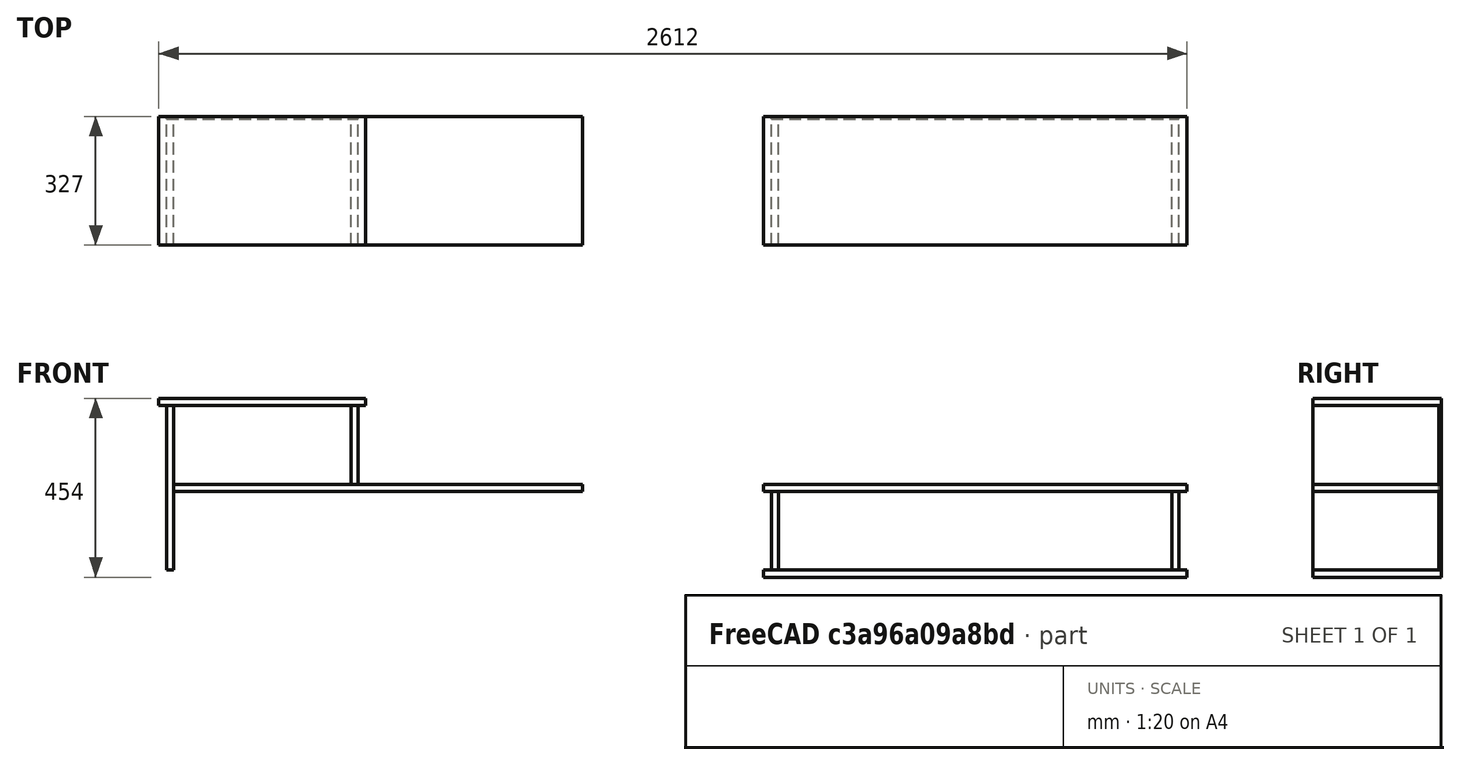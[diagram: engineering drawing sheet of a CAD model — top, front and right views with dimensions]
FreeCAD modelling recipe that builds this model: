
FCSTD DOCUMENT  (FreeCAD 0.20RUnknown)
Label: Brætspilsmøbel
License: All rights reserved
LicenseURL: http://en.wikipedia.org/wiki/All_rights_reserved
objects: Part::Box×7, Part::FeaturePython×6, Spreadsheet::Sheet×2, TechDraw::DrawSVGTemplate×1, TechDraw::DrawViewSpreadsheet×1, TechDraw::DrawPage×1
note: 13 computed .brp shape members not serialized (recipe doc carries the construction recipe); baked Part::Feature solids carry a one-line shape summary decoded from their .brp

FEATURE [Part::Box] panelYZ  label="Del1B2"
  AttacherType = Attacher::AttachEngine3D
  Height = 200
  Length = 486
  Placement = pos=(0,-7,236) rot=(0,0,1;0rad)
  Width = 7
  expr: .Placement.Base.y = -Spreadsheet.BagpladeT
  expr: .Placement.Base.z = <<maal>>.PladeT * 2 + <<maal>>.RumH
  expr: Height = <<maal>>.RumH
  expr: Length = <<maal>>.RumB + 2 * <<maal>>.PladeT
  expr: Width = Spreadsheet.BagpladeT
FEATURE [Spreadsheet::Sheet] Spreadsheet  label="maal"
  cells = A1=Rum b; B1=Rum h; C1=Rum d; D1=Plade tyk; E1=Bagplade tyk; F1=Underrum B; A2(RumB)==450mm; B2(RumH)==200mm; C2(RumD)==320mm; D2(PladeT)==18mm; E2(BagpladeT)==7mm; F2(UnderrumB)==1000mm; A5=Total bredde; B5=Total højde; C5=Total T; E5=OverUnderMarginB; A6(TotalB)==F2 + D2 * 2; B6(TotalH)==B2 * 2 + D2 * 3; C6(TotalT)==BagpladeT + RumD; E6(OverUnderMarginB)==20mm; A8=Del2X; A9(Del2X)==A6 + 500mm
FEATURE [Part::Box] panelZY  label="Del1L"
  AttacherType = Attacher::AttachEngine3D
  Height = 418
  Length = 18
  Placement = pos=(0,-327,18) rot=(0,0,1;0rad)
  Width = 320
  expr: .Placement.Base.y = -<<maal>>.TotalT
  expr: .Placement.Base.z = <<maal>>.PladeT
  expr: Height = <<maal>>.TotalH - <<maal>>.PladeT * 2
  expr: Length = <<maal>>.PladeT
  expr: Width = <<maal>>.RumD
FEATURE [Part::Box] panelXY  label="Del1U"
  AttacherType = Attacher::AttachEngine3D
  Height = 18
  Length = 1076
  Placement = pos=(-20,-327,0) rot=(0,0,1;0rad)
  Width = 327
  expr: .Placement.Base.x = -<<maal>>.OverUnderMarginB
  expr: .Placement.Base.y = -<<maal>>.TotalT
  expr: Height = <<maal>>.PladeT
  expr: Length = <<maal>>.TotalB + <<maal>>.OverUnderMarginB * 2
  expr: Width = <<maal>>.RumD + <<maal>>.BagpladeT
FEATURE [Part::Box] panelZY001  label="Del1R1"
  AttacherType = Attacher::AttachEngine3D
  Height = 200
  Length = 18
  Placement = pos=(1018,-327,18) rot=(0,0,1;0rad)
  Width = 320
  expr: .Placement.Base.x = <<maal>>.TotalB - <<maal>>.PladeT
  expr: .Placement.Base.y = -<<maal>>.TotalT
  expr: .Placement.Base.z = <<maal>>.PladeT
  expr: Height = <<maal>>.RumH
  expr: Length = <<maal>>.PladeT
  expr: Width = <<maal>>.RumD
FEATURE [Part::Box] panelXY001  label="Del1H"
  AttacherType = Attacher::AttachEngine3D
  Height = 18
  Length = 1038
  Placement = pos=(18,-327,218) rot=(0,0,1;0rad)
  Width = 327
  expr: .Placement.Base.x = <<maal>>.PladeT
  expr: .Placement.Base.y = -<<maal>>.TotalT
  expr: .Placement.Base.z = <<maal>>.RumH + <<maal>>.PladeT
  expr: Height = <<maal>>.PladeT
  expr: Length = <<maal>>.TotalB - <<maal>>.PladeT + <<maal>>.OverUnderMarginB
  expr: Width = <<maal>>.RumD + <<maal>>.BagpladeT
FEATURE [Part::FeaturePython] Clone  label="Del1R2"  # Draft clone (typed FeaturePython)
  AttacherType = Attacher::AttachEngine3D
  Fuse = false
  Objects = -> [panelZY001]
  Placement = pos=(468,-327,236) rot=(0,0,1;0rad)
  Scale = (1,1,1)
  expr: .Placement.Base.x = <<maal>>.RumB + <<maal>>.PladeT
  expr: .Placement.Base.y = -<<maal>>.BagpladeT - <<maal>>.RumD
  expr: .Placement.Base.z = <<maal>>.RumH + <<maal>>.PladeT * 2
FEATURE [Part::Box] panelXY002  label="Del1O"
  AttacherType = Attacher::AttachEngine3D
  Height = 18
  Length = 526
  Placement = pos=(-20,-327,436) rot=(0,0,1;0rad)
  Width = 327
  expr: .Placement.Base.x = -<<maal>>.OverUnderMarginB
  expr: .Placement.Base.y = -<<maal>>.TotalT
  expr: .Placement.Base.z = <<maal>>.TotalH - <<maal>>.PladeT
  expr: Height = <<maal>>.PladeT
  expr: Length = <<maal>>.RumB + <<maal>>.PladeT * 2 + <<maal>>.OverUnderMarginB * 2
  expr: Width = <<maal>>.RumD + <<maal>>.BagpladeT
FEATURE [Part::Box] panelYZ001  label="Del1B1"
  AttacherType = Attacher::AttachEngine3D
  Height = 200
  Length = 1036
  Placement = pos=(0,-7,18) rot=(0,0,1;0rad)
  Width = 7
  expr: .Placement.Base.y = -Spreadsheet.BagpladeT
  expr: .Placement.Base.z = <<maal>>.PladeT
  expr: Height = <<maal>>.RumH
  expr: Length = <<maal>>.TotalB
  expr: Width = Spreadsheet.BagpladeT
FEATURE [Part::FeaturePython] Clone001  label="Del2U"  # Draft clone (typed FeaturePython)
  AttacherType = Attacher::AttachEngine3D
  Fuse = false
  Objects = -> [panelXY]
  Placement = pos=(1516,-327,0) rot=(0,0,1;0rad)
  Scale = (1,1,1)
  expr: .Placement.Base.x = <<maal>>.Del2X - <<maal>>.OverUnderMarginB
  expr: .Placement.Base.y = -<<maal>>.BagpladeT - <<maal>>.RumD
FEATURE [Part::FeaturePython] Clone002  label="Del2O"  # Draft clone (typed FeaturePython)
  AttacherType = Attacher::AttachEngine3D
  Fuse = false
  Objects = -> [panelXY]
  Placement = pos=(1516,-327,218) rot=(0,0,1;0rad)
  Scale = (1,1,1)
  expr: .Placement.Base.x = <<maal>>.Del2X - <<maal>>.OverUnderMarginB
  expr: .Placement.Base.y = -<<maal>>.BagpladeT - <<maal>>.RumD
  expr: .Placement.Base.z = <<maal>>.RumH + <<maal>>.PladeT
FEATURE [Part::FeaturePython] Clone003  label="Del2L"  # Draft clone (typed FeaturePython)
  AttacherType = Attacher::AttachEngine3D
  Fuse = false
  Objects = -> [panelZY001]
  Placement = pos=(1536,-327,18) rot=(0,0,1;0rad)
  Scale = (1,1,1)
  expr: .Placement.Base.x = <<maal>>.Del2X
  expr: .Placement.Base.y = -<<maal>>.BagpladeT - <<maal>>.RumD
  expr: .Placement.Base.z = <<maal>>.PladeT
FEATURE [Part::FeaturePython] Clone004  label="Del2R"  # Draft clone (typed FeaturePython)
  AttacherType = Attacher::AttachEngine3D
  Fuse = false
  Objects = -> [panelZY001]
  Placement = pos=(2554,-327,18) rot=(0,0,1;0rad)
  Scale = (1,1,1)
  expr: .Placement.Base.x = <<maal>>.Del2X + <<maal>>.UnderrumB + <<maal>>.PladeT
  expr: .Placement.Base.y = -<<maal>>.BagpladeT - <<maal>>.RumD
  expr: .Placement.Base.z = <<maal>>.PladeT
FEATURE [Part::FeaturePython] Clone005  label="Del2B"  # Draft clone (typed FeaturePython)
  AttacherType = Attacher::AttachEngine3D
  Fuse = false
  Objects = -> [panelYZ001]
  Placement = pos=(1536,-7,18) rot=(0,0,1;0rad)
  Scale = (1,1,1)
  expr: .Placement.Base.x = <<maal>>.Del2X
  expr: .Placement.Base.y = -<<maal>>.BagpladeT
  expr: .Placement.Base.z = <<maal>>.PladeT
FEATURE [Spreadsheet::Sheet] toCut
  cells = A1=Quantity; C1=Dimensions; F1=Thickness; G1=m2; A2=1 x; C2=200 mm; D2=x; E2=486 mm; F2=7 mm; G2=0.09719999999999999; A3=1 x; C3=320 mm; D3=x; E3=418 mm; F3=18 mm; G3=0.13376; A4=3 x; C4=327 mm; D4=x; E4=1076 mm; F4=18 mm; G4=1.055556; A5=4 x; C5=200 mm; D5=x; E5=320 mm; F5=18 mm; G5=0.256; A6=1 x; C6=327 mm; D6=x; E6=1038 mm; F6=18 mm; G6=0.339426; A7=1 x; C7=327 mm; D7=x; E7=526 mm; F7=18 mm; G7=0.172002; A8=2 x; C8=200 mm; D8=x; E8=1036 mm; F8=7 mm; G8=0.4144; A9=Summary by thickness; A10=3 x; F10=7 mm; G10=0.5116000000000001; A11=10 x; F11=18 mm; G11=1.956744; A13=Edge size; G13=24.806 m; A15=Generated by FreeCAD macro: github.com/dprojects/getDimensions
FEATURE [TechDraw::DrawSVGTemplate] Template
  Height = 297
  Orientation = 0
  Width = 210
FEATURE [TechDraw::DrawViewSpreadsheet] Sheet
  CellEnd = G16
  CellStart = A1
  Font = DejaVu Sans
  LineWidth = 0.1
  LockPosition = false
  Rotation = 0
  ScaleType = 2
  Source = -> toCut
  Symbol = <blob: 15650 chars omitted>
  TextSize = 13
  X = 105
  Y = 148
FEATURE [TechDraw::DrawPage] toPrint
  KeepUpdated = true
  NextBalloonIndex = 1
  ProjectionType = 0
  Template = -> Template
  Views = -> [Sheet]
